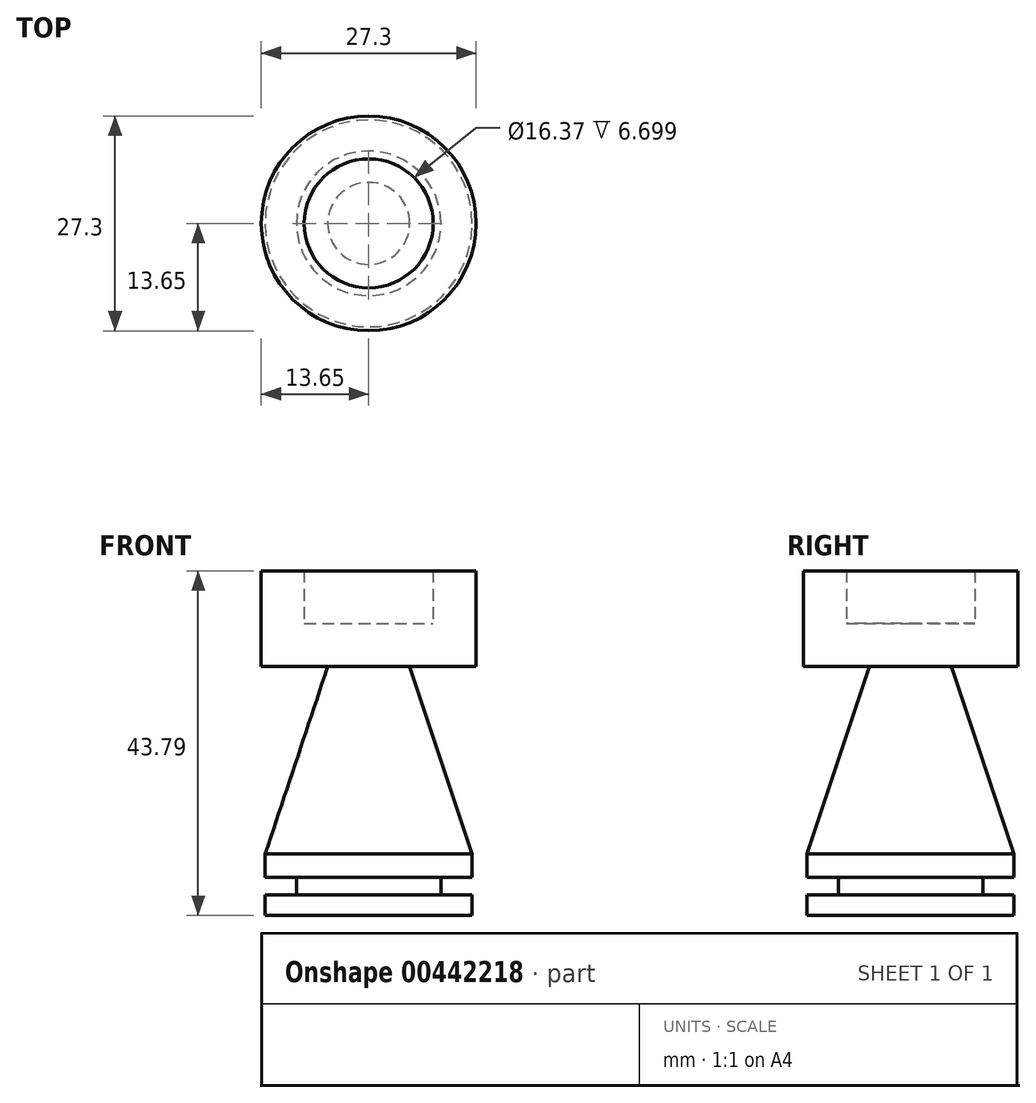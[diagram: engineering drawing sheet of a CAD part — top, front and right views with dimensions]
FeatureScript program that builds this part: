
annotation { "Feature Type Name" : "Feature", "Feature Type Description" : "" }
export const myFeature = defineFeature(function(context is Context, id is Id, definition is map)
    precondition{}
    {
        {
            var Q0;
            Q0=qCreatedBy(makeId("Right.planeOp"),FACE);
            var sketch = newSketch(context, id + "F0", { "sketchPlane" : qUnion([Q0])});
            skLineSegment(sketch, "E0", {"start": v(0, 0) * mm, "end": v(0, 37.09) * mm});
            skLineSegment(sketch, "E1", {"start": v(0, 37.09) * mm, "end": v(8.19, 37.09) * mm});
            skLineSegment(sketch, "E2", {"start": v(8.19, 37.09) * mm, "end": v(8.19, 43.79) * mm});
            skLineSegment(sketch, "E3", {"start": v(8.19, 43.79) * mm, "end": v(13.65, 43.79) * mm});
            skLineSegment(sketch, "E4", {"start": v(13.65, 43.79) * mm, "end": v(13.65, 31.63) * mm});
            skLineSegment(sketch, "E5", {"start": v(13.65, 31.63) * mm, "end": v(5.2, 31.63) * mm});
            skLineSegment(sketch, "E6", {"start": v(5.2, 31.63) * mm, "end": v(13.15, 7.81) * mm});
            skLineSegment(sketch, "E7", {"start": v(13.15, 7.81) * mm, "end": v(13.15, 4.84) * mm});
            skLineSegment(sketch, "E8", {"start": v(13.15, 4.84) * mm, "end": v(9.18, 4.84) * mm});
            skLineSegment(sketch, "E9", {"start": v(9.18, 4.84) * mm, "end": v(9.18, 2.6) * mm});
            skLineSegment(sketch, "E10", {"start": v(8.93, 2.6) * mm, "end": v(13.15, 2.6) * mm});
            skLineSegment(sketch, "E11", {"start": v(13.15, 2.6) * mm, "end": v(13.15, 0) * mm});
            skLineSegment(sketch, "E12", {"start": v(13.15, 0) * mm, "end": v(0, 0) * mm});
            skSolve(sketch);
        }
        {
            var Q0;
            Q0=makeQuery(id+"F0.imprint","IMPRINT",FACE,{"disambiguationData":[TD([[makeQuery(id+"F0.imprint","IMPRINT",EDGE,{"derivedFrom":sQuery(id+"F0.wireOp",EDGE,"E0")}),-1.0]])]});
            var Q1;
            Q1=sQuery(id+"F0.wireOp",EDGE,"E0");
            revolve(context, id + "F1", {"entities" : qUnion([Q0]), "axis" : qUnion([Q1]), "revolveType" : RevolveType.FULL});
        }
    });
